annotation { "Feature Type Name" : "Feature", "Feature Type Description" : "" }
export const myFeature = defineFeature(function(context is Context, id is Id, definition is map)
    precondition{}
    {
        {
            var Q0;
            Q0=qCreatedBy(makeId("Front.planeOp"),FACE);
            var sketch = newSketch(context, id + "F0", { "sketchPlane" : qUnion([Q0])});
            skText(sketch, "E0", { "text": "Henry Craw\n1942-2013", "fontName": "OpenSans-Regular.ttf"});
            skLineSegment(sketch, "E1", {"start": v(-33.61, 9.93) * mm, "end": v(-33.61, -105.9) * mm});
            skLineSegment(sketch, "E2", {"start": v(-33.61, -105.9) * mm, "end": v(68.78, -105.9) * mm});
            skLineSegment(sketch, "E3", {"start": v(68.78, -105.9) * mm, "end": v(68.78, 9.1) * mm});
            skArc(sketch, "E4", {"start": v(68.78, 9.1) * mm, "mid": v(18, 60.3) * mm, "end": v(-33.61, 9.93) * mm});
            const initialGuessF0  = {"E0": [-0.01894, -0.00666, 1, 0, 0.00995]};
            skSetInitialGuess(sketch, initialGuessF0);
            skSolve(sketch);
        }
        {
            var Q0;
            Q0 = qSketchRegion(id + "F0", true);
            extrude(context, id + "F1", {"entities" : qUnion([Q0]), "oppositeDirection" : true, "depth" : 25.4 * mm});
        }
    });